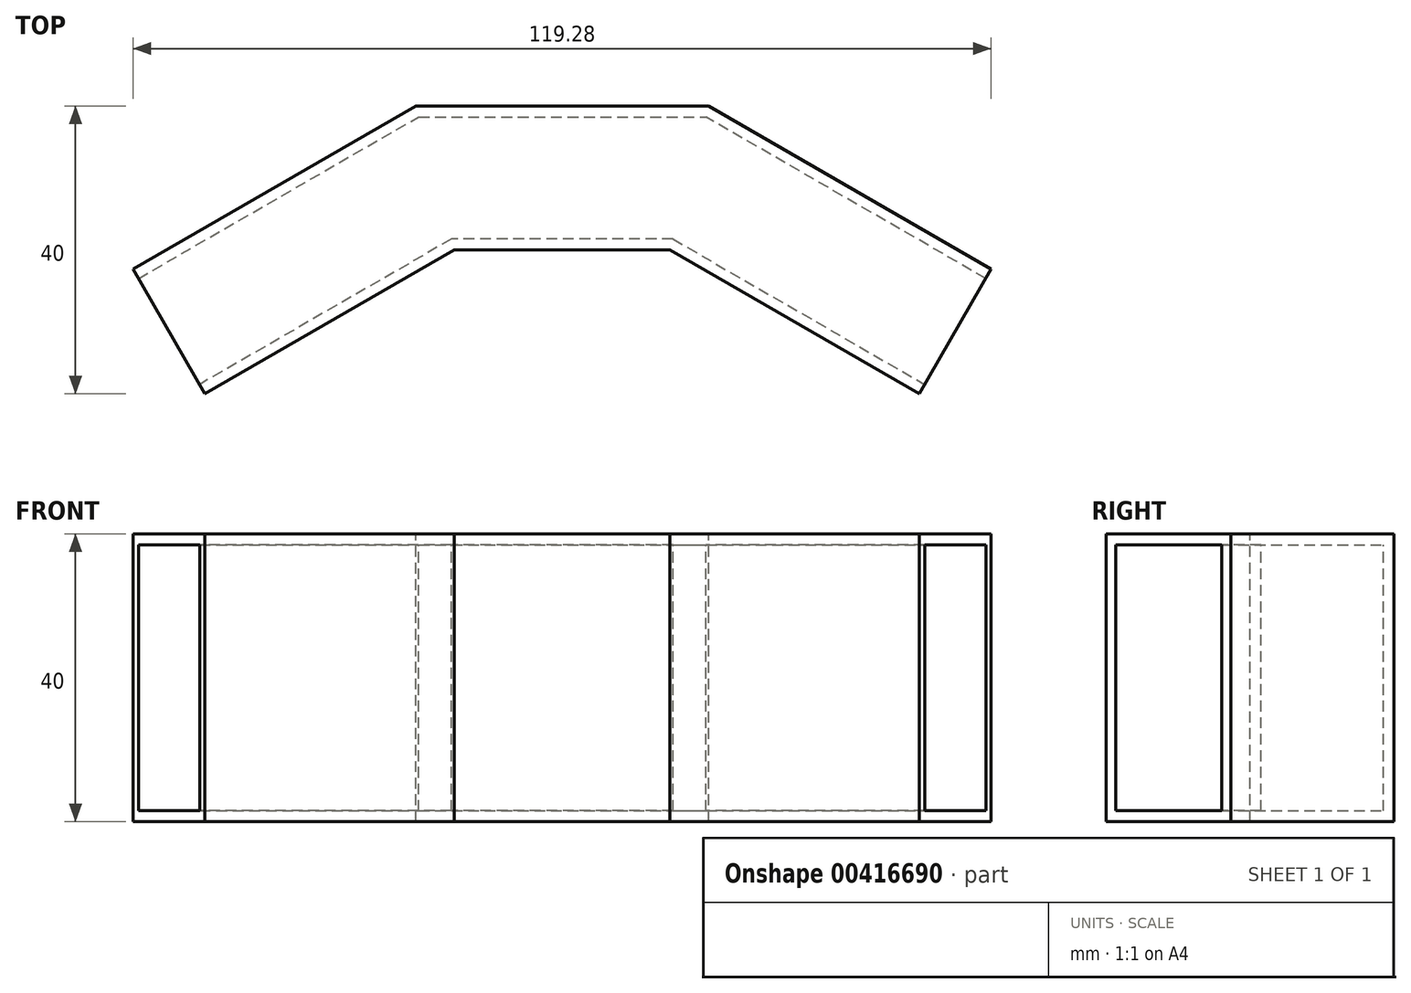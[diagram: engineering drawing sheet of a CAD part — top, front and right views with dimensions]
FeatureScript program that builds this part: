
annotation { "Feature Type Name" : "Feature", "Feature Type Description" : "" }
export const myFeature = defineFeature(function(context is Context, id is Id, definition is map)
    precondition{}
    {
        {
            var Q0;
            Q0=qCreatedBy(makeId("Top.planeOp"),FACE);
            var sketch = newSketch(context, id + "F0", { "sketchPlane" : qUnion([Q0])});
            skLineSegment(sketch, "E0", {"start": v(0, 0) * mm, "end": v(-15, 0) * mm});
            skLineSegment(sketch, "E1", {"start": v(0, 0) * mm, "end": v(15, 0) * mm});
            skLineSegment(sketch, "E2", {"start": v(-15, 0) * mm, "end": v(-49.64, -20) * mm});
            skLineSegment(sketch, "E3", {"start": v(15, 0) * mm, "end": v(49.64, -20) * mm});
            skLineSegment(sketch, "E4", {"start": v(-49.64, -20) * mm, "end": v(-59.64, -2.68) * mm});
            skLineSegment(sketch, "E5", {"start": v(49.64, -20) * mm, "end": v(59.64, -2.68) * mm});
            skLineSegment(sketch, "E6", {"start": v(0, 0) * mm, "end": v(0, 20) * mm, "construction": true});
            skLineSegment(sketch, "E7", {"start": v(0, 20) * mm, "end": v(-20.36, 20) * mm});
            skLineSegment(sketch, "E8", {"start": v(0, 20) * mm, "end": v(20.36, 20) * mm});
            skLineSegment(sketch, "E9", {"start": v(-59.64, -2.68) * mm, "end": v(-20.36, 20) * mm});
            skLineSegment(sketch, "E10", {"start": v(59.64, -2.68) * mm, "end": v(20.36, 20) * mm});
            skCircle(sketch, "E11", {"center": v(0, -89.49) * mm, "radius": 85 * mm, "construction": true});
            skCircle(sketch, "E12", {"center": v(0, -60.62) * mm, "radius": 60 * mm, "construction": true});
            skCircle(sketch, "E13", {"center": v(0, -72.17) * mm, "radius": 70 * mm, "construction": true});
            skSolve(sketch);
        }
        {
            var Q0;
            Q0=makeQuery(id+"F0.imprint","IMPRINT",FACE,{"disambiguationData":[TD([[makeQuery(id+"F0.imprint","IMPRINT",EDGE,{"derivedFrom":sQuery(id+"F0.wireOp",EDGE,"E0")}),-1.0]])]});
            extrude(context, id + "F1", {"entities" : qUnion([Q0]), "oppositeDirection" : true, "depth" : 40 * mm});
        }
        {
            var Q0;
            Q0=makeQuery(id+"F1.opExtrude","SWEPT_FACE",FACE,{"disambiguationData":[OSD([sQuery(id+"F0.wireOp",EDGE,"E4")])]});
            var Q1;
            Q1=makeQuery(id+"F1.opExtrude","SWEPT_FACE",FACE,{"disambiguationData":[OSD([sQuery(id+"F0.wireOp",EDGE,"E5")])]});
            shell(context, id + "F2", {"entities" : qUnion([Q0, Q1]), "thickness" : 1.5 * mm});
        }
    });
